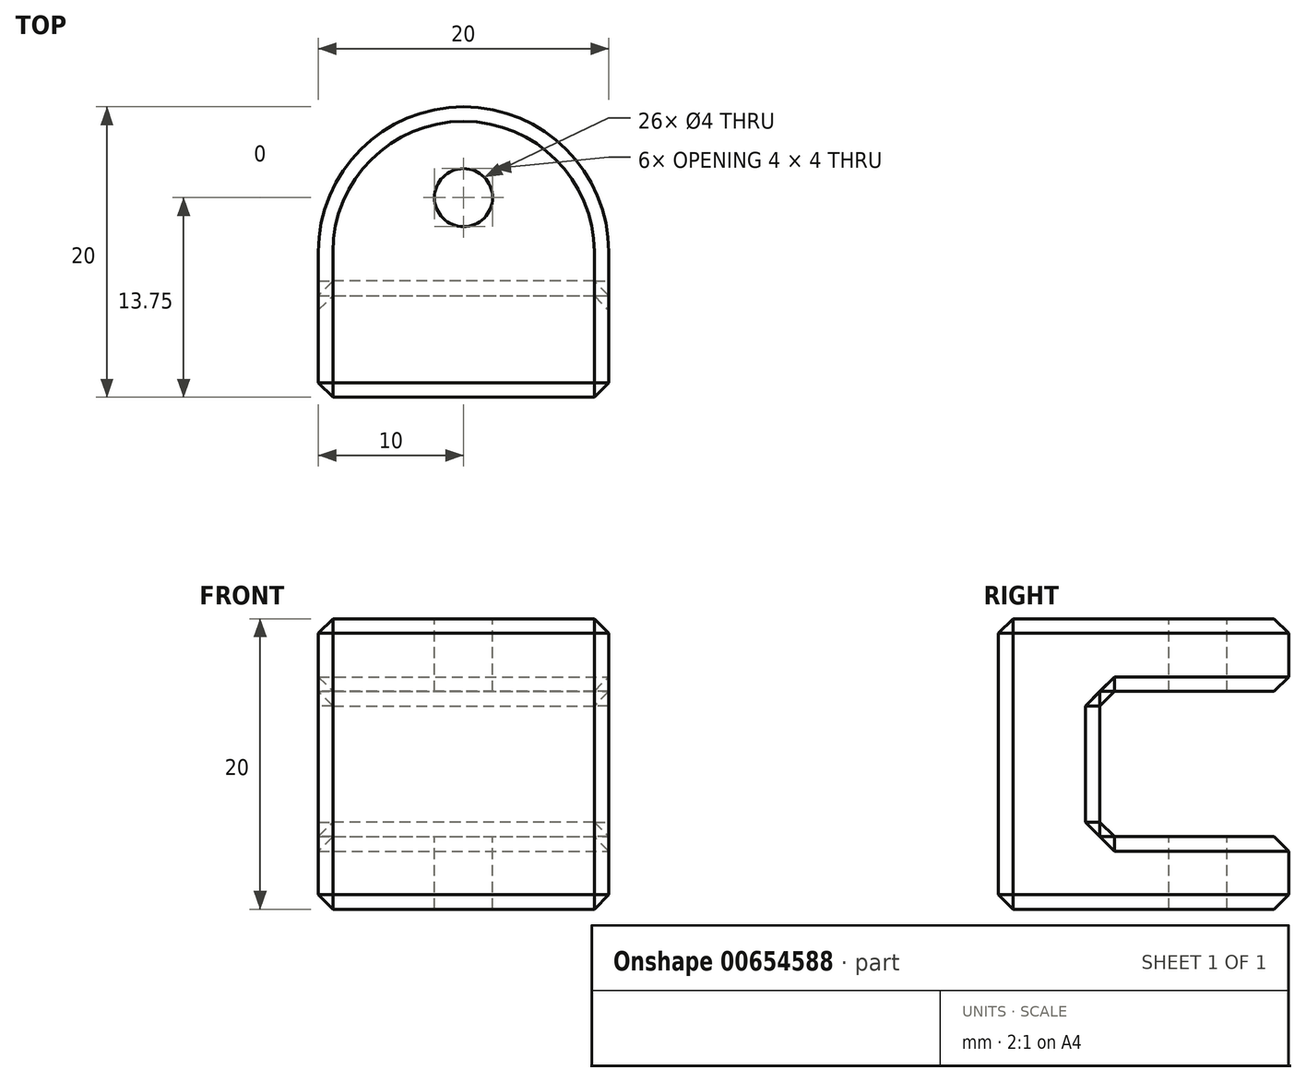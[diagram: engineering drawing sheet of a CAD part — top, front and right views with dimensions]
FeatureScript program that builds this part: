
annotation { "Feature Type Name" : "Feature", "Feature Type Description" : "" }
export const myFeature = defineFeature(function(context is Context, id is Id, definition is map)
    precondition{}
    {
        {
            var Q0;
            Q0=qCreatedBy(makeId("Front.planeOp"),FACE);
            var sketch = newSketch(context, id + "F0", { "sketchPlane" : qUnion([Q0])});
            skLineSegment(sketch, "E0.bottom", {"start": v(0, 0) * mm, "end": v(20, 0) * mm});
            skLineSegment(sketch, "E0.top", {"start": v(0, 20) * mm, "end": v(20, 20) * mm});
            skLineSegment(sketch, "E0.left", {"start": v(0, 0) * mm, "end": v(0, 20) * mm});
            skLineSegment(sketch, "E0.right", {"start": v(20, 0) * mm, "end": v(20, 20) * mm});
            skSolve(sketch);
        }
        {
            var Q0;
            Q0=makeQuery(id+"F0.imprint","IMPRINT",FACE,{"disambiguationData":[TD([[makeQuery(id+"F0.imprint","IMPRINT",EDGE,{"derivedFrom":sQuery(id+"F0.wireOp",EDGE,"E0.bottom")}),1.0]])]});
            extrude(context, id + "F1", {"entities" : qUnion([Q0]), "oppositeDirection" : true, "depth" : 20 * mm, "offsetDistance" : 25 * mm});
        }
        {
            var Q0;
            Q0=makeQuery(id+"F1.opExtrude","SWEPT_FACE",FACE,{"disambiguationData":[OSD([sQuery(id+"F0.wireOp",EDGE,"E0.right")])]});
            var sketch = newSketch(context, id + "F2", { "sketchPlane" : qUnion([Q0])});
            skLineSegment(sketch, "E1.bottom", {"start": v(7, 15) * mm, "end": v(20, 15) * mm});
            skLineSegment(sketch, "E1.top", {"start": v(7, 5) * mm, "end": v(20, 5) * mm});
            skLineSegment(sketch, "E1.left", {"start": v(7, 15) * mm, "end": v(7, 5) * mm});
            skLineSegment(sketch, "E1.right", {"start": v(20, 15) * mm, "end": v(20, 5) * mm});
            skSolve(sketch);
        }
        {
            var Q0;
            Q0=makeQuery(id+"F2.imprint","IMPRINT",FACE,{"disambiguationData":[TD([[makeQuery(id+"F2.imprint","IMPRINT",EDGE,{"derivedFrom":sQuery(id+"F2.wireOp",EDGE,"E1.bottom")}),-1.0]])]});
            extrude(context, id + "F3", {"entities" : qUnion([Q0]), "operationType" : NewBodyOperationType.REMOVE, "endBound" : BoundingType.UP_TO_NEXT, "oppositeDirection" : true, "depth" : 25 * mm, "offsetDistance" : 25 * mm});
        }
        {
            var Q0;
            Q0=makeQuery(id+"F1.opExtrude","SWEPT_FACE",FACE,{"disambiguationData":[OSD([sQuery(id+"F0.wireOp",EDGE,"E0.top")])]});
            var sketch = newSketch(context, id + "F4", { "sketchPlane" : qUnion([Q0])});
            skCircle(sketch, "E2", {"center": v(10, 13.75) * mm, "radius": 2 * mm});
            skSolve(sketch);
        }
        {
            var Q0;
            Q0=makeQuery(id+"F4.imprint","IMPRINT",FACE,{"disambiguationData":[TD([[makeQuery(id+"F4.imprint","IMPRINT",EDGE,{"derivedFrom":sQuery(id+"F4.wireOp",EDGE,"E2")}),1.0]])]});
            var Q1;
            Q1=makeQuery(id+"F1.opExtrude","SWEPT_FACE",FACE,{"disambiguationData":[OSD([sQuery(id+"F0.wireOp",EDGE,"E0.bottom")])]});
            extrude(context, id + "F5", {"entities" : qUnion([Q0]), "operationType" : NewBodyOperationType.REMOVE, "endBound" : BoundingType.UP_TO_SURFACE, "oppositeDirection" : true, "depth" : 25 * mm, "endBoundEntityFace" : qUnion([Q1]), "offsetDistance" : 25 * mm});
        }
        {
            var Q0;
            {var subQ0=sQuery(id+"F0.wireOp",EDGE,"E0.bottom");var subQ1=sQuery(id+"F0.wireOp",EDGE,"E0.left");Q0=makeQuery(id+"F3.boolean.opBoolean","SPLIT",EDGE,{"disambiguationData":[TD([makeQuery(id+"F1.opExtrude","SWEPT_FACE",FACE,{"disambiguationData":[OSD([subQ0])]})])],"derivedFrom":makeQuery(id+"F1.opExtrude","CAP_EDGE",EDGE,{"disambiguationData":[OSD([subQ1])],"isStart":false})});}
            var Q1;
            {var subQ0=sQuery(id+"F0.wireOp",EDGE,"E0.bottom");var subQ1=sQuery(id+"F0.wireOp",EDGE,"E0.right");Q1=makeQuery(id+"F3.boolean.opBoolean","SPLIT",EDGE,{"disambiguationData":[TD([makeQuery(id+"F1.opExtrude","SWEPT_FACE",FACE,{"disambiguationData":[OSD([subQ0])]})])],"derivedFrom":makeQuery(id+"F1.opExtrude","CAP_EDGE",EDGE,{"disambiguationData":[OSD([subQ1])],"isStart":false})});}
            var Q2;
            {var subQ0=sQuery(id+"F0.wireOp",EDGE,"E0.right");var subQ1=sQuery(id+"F0.wireOp",EDGE,"E0.top");Q2=makeQuery(id+"F3.boolean.opBoolean","SPLIT",EDGE,{"disambiguationData":[TD([makeQuery(id+"F1.opExtrude","SWEPT_FACE",FACE,{"disambiguationData":[OSD([subQ1])]})])],"derivedFrom":makeQuery(id+"F1.opExtrude","CAP_EDGE",EDGE,{"disambiguationData":[OSD([subQ0])],"isStart":false})});}
            var Q3;
            {var subQ0=sQuery(id+"F0.wireOp",EDGE,"E0.left");var subQ1=sQuery(id+"F0.wireOp",EDGE,"E0.top");Q3=makeQuery(id+"F3.boolean.opBoolean","SPLIT",EDGE,{"disambiguationData":[TD([makeQuery(id+"F1.opExtrude","SWEPT_FACE",FACE,{"disambiguationData":[OSD([subQ1])]})])],"derivedFrom":makeQuery(id+"F1.opExtrude","CAP_EDGE",EDGE,{"disambiguationData":[OSD([subQ0])],"isStart":false})});}
            fillet(context, id + "F6", {"entities" : qUnion([Q0, Q1, Q2, Q3]), "radius" : 10 * mm, "tangentPropagation" : true, "allowEdgeOverflow" : false});
        }
        {
            var Q0;
            Q0=makeQuery(id+"F1.opExtrude","CAP_FACE",FACE,{"disambiguationData":[OSD([sQuery(id+"F0.wireOp",EDGE,"E0.bottom"),sQuery(id+"F0.wireOp",EDGE,"E0.top"),sQuery(id+"F0.wireOp",EDGE,"E0.left"),sQuery(id+"F0.wireOp",EDGE,"E0.right")])],"isStart":true});
            var Q1;
            Q1=makeQuery(id+"F3.boolean.opBoolean","COPY",FACE,{"derivedFrom":makeQuery(id+"F3.opExtrude","SWEPT_FACE",FACE,{"disambiguationData":[OSD([sQuery(id+"F2.wireOp",EDGE,"E1.left")])]})});
            var Q2;
            {var subQ0=sQuery(id+"F0.wireOp",EDGE,"E0.bottom");var subQ1=sQuery(id+"F0.wireOp",EDGE,"E0.right");Q2=makeQuery(id+"F6.opFillet","BLEND_FACE",FACE,{"disambiguationData":[OSD([subQ1]),TDD([makeQuery(id+"F3.boolean.opBoolean","SPLIT",EDGE,{"disambiguationData":[TD([makeQuery(id+"F1.opExtrude","SWEPT_FACE",FACE,{"disambiguationData":[OSD([subQ0])]})])],"derivedFrom":makeQuery(id+"F1.opExtrude","CAP_EDGE",EDGE,{"disambiguationData":[OSD([subQ1])],"isStart":false})})])]});}
            var Q3;
            Q3=makeQuery(id+"F1.opExtrude","SWEPT_FACE",FACE,{"disambiguationData":[OSD([sQuery(id+"F0.wireOp",EDGE,"E0.right")])]});
            var Q4;
            {var subQ0=sQuery(id+"F0.wireOp",EDGE,"E0.right");var subQ1=sQuery(id+"F0.wireOp",EDGE,"E0.top");Q4=makeQuery(id+"F6.opFillet","BLEND_FACE",FACE,{"disambiguationData":[OSD([subQ0]),TDD([makeQuery(id+"F3.boolean.opBoolean","SPLIT",EDGE,{"disambiguationData":[TD([makeQuery(id+"F1.opExtrude","SWEPT_FACE",FACE,{"disambiguationData":[OSD([subQ1])]})])],"derivedFrom":makeQuery(id+"F1.opExtrude","CAP_EDGE",EDGE,{"disambiguationData":[OSD([subQ0])],"isStart":false})})])]});}
            chamfer(context, id + "F7", {"entities" : qUnion([Q0, Q1, Q2, Q3, Q4]), "width" : 1 * mm, "tangentPropagation" : true});
        }
    });
